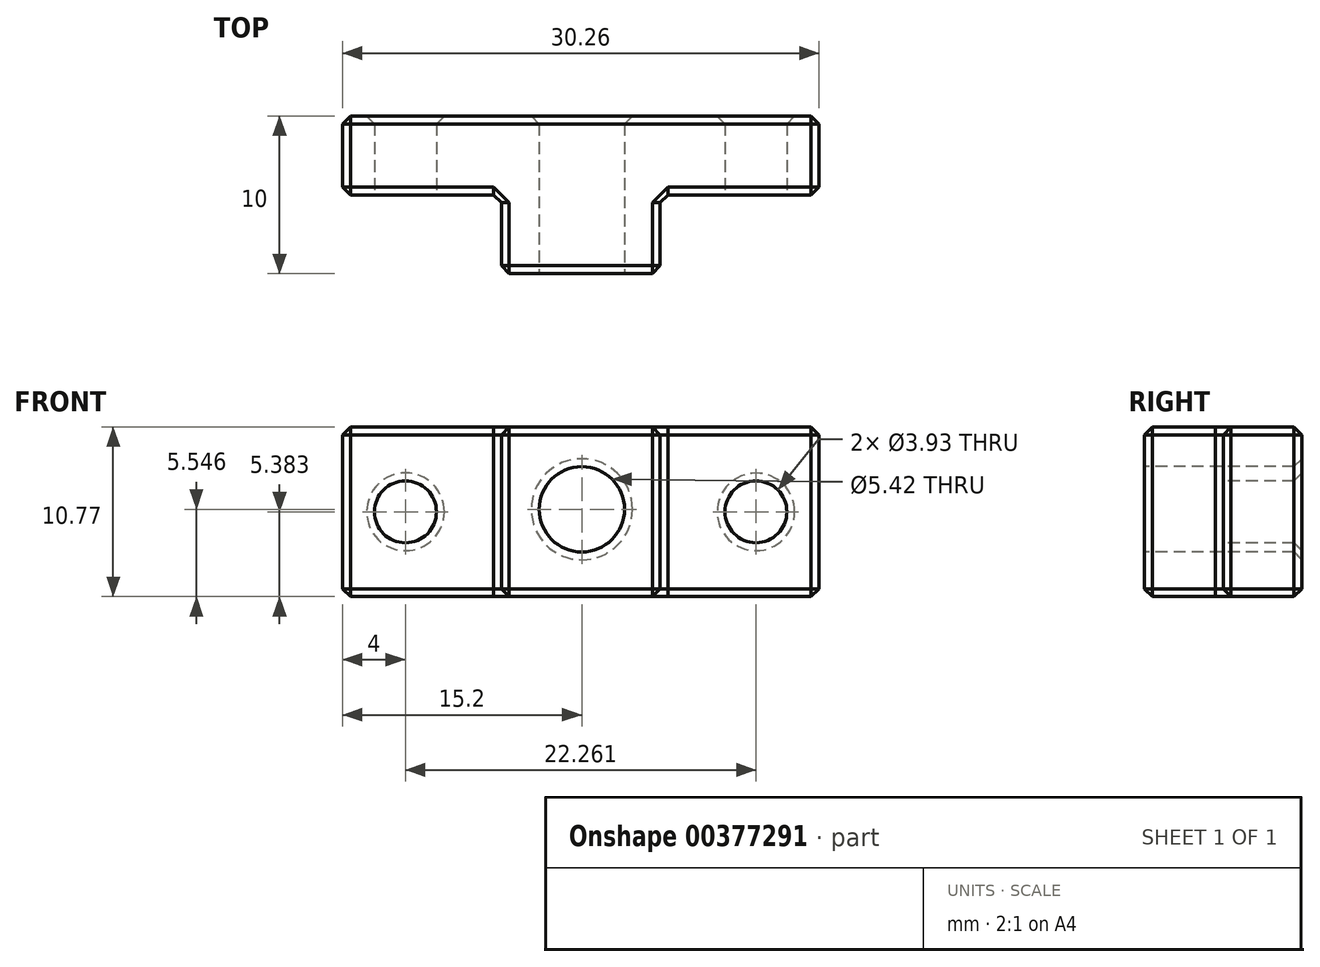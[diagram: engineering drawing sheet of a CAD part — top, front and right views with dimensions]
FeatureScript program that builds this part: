
annotation { "Feature Type Name" : "Feature", "Feature Type Description" : "" }
export const myFeature = defineFeature(function(context is Context, id is Id, definition is map)
    precondition{}
    {
        {
            var Q0;
            Q0=qCreatedBy(makeId("Front.planeOp"),FACE);
            var sketch = newSketch(context, id + "F0", { "sketchPlane" : qUnion([Q0])});
            skLineSegment(sketch, "E0.bottom", {"start": v(0, 0) * mm, "end": v(30.26, 0) * mm});
            skLineSegment(sketch, "E0.top", {"start": v(0, -10.77) * mm, "end": v(30.26, -10.77) * mm});
            skLineSegment(sketch, "E0.left", {"start": v(0, 0) * mm, "end": v(0, -10.77) * mm});
            skLineSegment(sketch, "E0.right", {"start": v(30.26, 0) * mm, "end": v(30.26, -10.77) * mm});
            skSolve(sketch);
        }
        {
            var Q0;
            Q0 = qSketchRegion(id + "F0", true);
            extrude(context, id + "F1", {"entities" : qUnion([Q0]), "depth" : 10 * mm});
        }
        {
            var Q0;
            Q0=makeQuery(id+"F1.opExtrude","CAP_FACE",FACE,{"disambiguationData":[OSD([sQuery(id+"F0.wireOp",EDGE,"E0.bottom"),sQuery(id+"F0.wireOp",EDGE,"E0.top"),sQuery(id+"F0.wireOp",EDGE,"E0.left"),sQuery(id+"F0.wireOp",EDGE,"E0.right")])],"isStart":false});
            var sketch = newSketch(context, id + "F2", { "sketchPlane" : qUnion([Q0])});
            skLineSegment(sketch, "E1.bottom", {"start": v(0, 0) * mm, "end": v(10.05, 0) * mm});
            skLineSegment(sketch, "E1.top", {"start": v(0, -10.77) * mm, "end": v(10.05, -10.77) * mm});
            skLineSegment(sketch, "E1.left", {"start": v(0, 0) * mm, "end": v(0, -10.77) * mm});
            skLineSegment(sketch, "E1.right", {"start": v(10.05, 0) * mm, "end": v(10.05, -10.77) * mm});
            skSolve(sketch);
        }
        {
            var Q0;
            Q0 = qSketchRegion(id + "F2", true);
            extrude(context, id + "F3", {"entities" : qUnion([Q0]), "operationType" : NewBodyOperationType.ADD, "depth" : -5 * mm});
        }
        {
            var Q0;
            Q0=makeQuery(id+"F1.opExtrude","CAP_FACE",FACE,{"disambiguationData":[OSD([sQuery(id+"F0.wireOp",EDGE,"E0.bottom"),sQuery(id+"F0.wireOp",EDGE,"E0.top"),sQuery(id+"F0.wireOp",EDGE,"E0.left"),sQuery(id+"F0.wireOp",EDGE,"E0.right")])],"isStart":false});
            var sketch = newSketch(context, id + "F4", { "sketchPlane" : qUnion([Q0])});
            skLineSegment(sketch, "E2.bottom", {"start": v(0, 0) * mm, "end": v(10.1, 0) * mm});
            skLineSegment(sketch, "E2.top", {"start": v(0, -10.77) * mm, "end": v(10.1, -10.77) * mm});
            skLineSegment(sketch, "E2.left", {"start": v(0, 0) * mm, "end": v(0, -10.77) * mm});
            skLineSegment(sketch, "E2.right", {"start": v(10.1, 0) * mm, "end": v(10.1, -10.77) * mm});
            skSolve(sketch);
        }
        {
            var Q0;
            Q0=makeQuery(id+"F4.imprint","IMPRINT",FACE,{"disambiguationData":[TD([[makeQuery(id+"F4.imprint","IMPRINT",EDGE,{"derivedFrom":sQuery(id+"F4.wireOp",EDGE,"E2.bottom")}),-1.0]])]});
            extrude(context, id + "F5", {"entities" : qUnion([Q0]), "operationType" : NewBodyOperationType.REMOVE, "oppositeDirection" : true, "depth" : 5 * mm});
        }
        {
            var Q0;
            Q0=makeQuery(id+"F1.opExtrude","CAP_FACE",FACE,{"disambiguationData":[OSD([sQuery(id+"F0.wireOp",EDGE,"E0.bottom"),sQuery(id+"F0.wireOp",EDGE,"E0.top"),sQuery(id+"F0.wireOp",EDGE,"E0.left"),sQuery(id+"F0.wireOp",EDGE,"E0.right")])],"isStart":false});
            var sketch = newSketch(context, id + "F6", { "sketchPlane" : qUnion([Q0])});
            skLineSegment(sketch, "E3.bottom", {"start": v(30.26, 0) * mm, "end": v(20.18, 0) * mm});
            skLineSegment(sketch, "E3.top", {"start": v(30.26, -10.77) * mm, "end": v(20.18, -10.77) * mm});
            skLineSegment(sketch, "E3.left", {"start": v(30.26, 0) * mm, "end": v(30.26, -10.77) * mm});
            skLineSegment(sketch, "E3.right", {"start": v(20.18, 0) * mm, "end": v(20.18, -10.77) * mm});
            skSolve(sketch);
        }
        {
            var Q0;
            Q0 = qSketchRegion(id + "F6", true);
            extrude(context, id + "F7", {"entities" : qUnion([Q0]), "operationType" : NewBodyOperationType.REMOVE, "oppositeDirection" : true, "depth" : 5 * mm});
        }
        {
            var Q0;
            Q0=makeQuery(id+"F1.opExtrude","CAP_FACE",FACE,{"disambiguationData":[OSD([sQuery(id+"F0.wireOp",EDGE,"E0.bottom"),sQuery(id+"F0.wireOp",EDGE,"E0.top"),sQuery(id+"F0.wireOp",EDGE,"E0.left"),sQuery(id+"F0.wireOp",EDGE,"E0.right")])],"isStart":false});
            var sketch = newSketch(context, id + "F8", { "sketchPlane" : qUnion([Q0])});
            skCircle(sketch, "E4", {"center": v(15.2, -5.22) * mm, "radius": 2.71 * mm});
            skSolve(sketch);
        }
        {
            var Q0;
            Q0 = qSketchRegion(id + "F8", true);
            extrude(context, id + "F9", {"entities" : qUnion([Q0]), "operationType" : NewBodyOperationType.REMOVE, "oppositeDirection" : true, "depth" : 25 * mm});
        }
        {
            var Q0;
            Q0=makeQuery(id+"F5.boolean.opBoolean","COPY",FACE,{"derivedFrom":makeQuery(id+"F5.opExtrude","CAP_FACE",FACE,{"disambiguationData":[OSD([sQuery(id+"F4.wireOp",EDGE,"E2.bottom"),sQuery(id+"F4.wireOp",EDGE,"E2.top"),sQuery(id+"F4.wireOp",EDGE,"E2.left"),sQuery(id+"F4.wireOp",EDGE,"E2.right")])],"isStart":false})});
            var sketch = newSketch(context, id + "F10", { "sketchPlane" : qUnion([Q0])});
            skLineSegment(sketch, "E5", {"start": v(4, 0) * mm, "end": v(4, -10.77) * mm});
            skCircle(sketch, "E6", {"center": v(4, -5.39) * mm, "radius": 1.97 * mm});
            skSolve(sketch);
        }
        {
            var Q0;
            Q0 = qSketchRegion(id + "F10", true);
            extrude(context, id + "F11", {"entities" : qUnion([Q0]), "operationType" : NewBodyOperationType.REMOVE, "oppositeDirection" : true, "depth" : 25 * mm});
        }
        {
            var Q0;
            Q0=makeQuery(id+"F7.boolean.opBoolean","COPY",FACE,{"derivedFrom":makeQuery(id+"F7.opExtrude","CAP_FACE",FACE,{"disambiguationData":[OSD([sQuery(id+"F6.wireOp",EDGE,"E3.bottom"),sQuery(id+"F6.wireOp",EDGE,"E3.top"),sQuery(id+"F6.wireOp",EDGE,"E3.left"),sQuery(id+"F6.wireOp",EDGE,"E3.right")])],"isStart":false})});
            var sketch = newSketch(context, id + "F12", { "sketchPlane" : qUnion([Q0])});
            skLineSegment(sketch, "E7", {"start": v(26.26, 0) * mm, "end": v(26.26, -10.77) * mm});
            skCircle(sketch, "E8", {"center": v(26.26, -5.39) * mm, "radius": 1.96 * mm});
            skSolve(sketch);
        }
        {
            var Q0;
            Q0 = qSketchRegion(id + "F12", true);
            extrude(context, id + "F13", {"entities" : qUnion([Q0]), "operationType" : NewBodyOperationType.REMOVE, "oppositeDirection" : true, "depth" : 25 * mm});
        }
        {
            var Q0;
            Q0=makeQuery(id+"F9.boolean.opBoolean","COPY",EDGE,{"derivedFrom":makeQuery(id+"F9.opExtrude","CAP_EDGE",EDGE,{"disambiguationData":[OSD([sQuery(id+"F8.wireOp",EDGE,"E4")])],"isStart":true})});
            var Q1;
            Q1=makeQuery(id+"F13.boolean.opBoolean","COPY",EDGE,{"derivedFrom":makeQuery(id+"F13.opExtrude","CAP_EDGE",EDGE,{"disambiguationData":[OSD([sQuery(id+"F12.wireOp",EDGE,"E8")])],"isStart":true})});
            var Q2;
            Q2=makeQuery(id+"F11.boolean.opBoolean","COPY",EDGE,{"derivedFrom":makeQuery(id+"F11.opExtrude","CAP_EDGE",EDGE,{"disambiguationData":[OSD([sQuery(id+"F10.wireOp",EDGE,"E6")])],"isStart":true})});
            var Q3;
            Q3=makeQuery(id+"F5.boolean.opBoolean","COPY",FACE,{"derivedFrom":makeQuery(id+"F5.opExtrude","SWEPT_FACE",FACE,{"disambiguationData":[OSD([sQuery(id+"F4.wireOp",EDGE,"E2.right")])]})});
            var Q4;
            Q4=makeQuery(id+"F1.opExtrude","SWEPT_FACE",FACE,{"disambiguationData":[OSD([sQuery(id+"F0.wireOp",EDGE,"E0.top")])]});
            var Q5;
            Q5=makeQuery(id+"F1.opExtrude","SWEPT_FACE",FACE,{"disambiguationData":[OSD([sQuery(id+"F0.wireOp",EDGE,"E0.left")])]});
            var Q6;
            Q6=makeQuery(id+"F1.opExtrude","SWEPT_FACE",FACE,{"disambiguationData":[OSD([sQuery(id+"F0.wireOp",EDGE,"E0.bottom")])]});
            var Q7;
            Q7=makeQuery(id+"F7.boolean.opBoolean","COPY",FACE,{"derivedFrom":makeQuery(id+"F7.opExtrude","SWEPT_FACE",FACE,{"disambiguationData":[OSD([sQuery(id+"F6.wireOp",EDGE,"E3.right")])]})});
            var Q8;
            Q8=makeQuery(id+"F1.opExtrude","SWEPT_FACE",FACE,{"disambiguationData":[OSD([sQuery(id+"F0.wireOp",EDGE,"E0.right")])]});
            var Q9;
            Q9=makeQuery(id+"F1.opExtrude","CAP_FACE",FACE,{"disambiguationData":[OSD([sQuery(id+"F0.wireOp",EDGE,"E0.bottom"),sQuery(id+"F0.wireOp",EDGE,"E0.top"),sQuery(id+"F0.wireOp",EDGE,"E0.left"),sQuery(id+"F0.wireOp",EDGE,"E0.right")])],"isStart":true});
            chamfer(context, id + "F14", {"entities" : qUnion([Q0, Q1, Q2, Q3, Q4, Q5, Q6, Q7, Q8, Q9]), "width" : 0.5 * mm, "tangentPropagation" : true});
        }
    });
